# Revit family: Lighting-ArredoUrbano-GEWISS-EXTRO-BASE_COLONNA
name_source: partatom
category: Apparecchi per illuminazione
units: mm (PartAtom-declared; Revit-internal decimal feet)

## family parameters
Basato su piano di lavoro = Sì
Condiviso = No
Numero OmniClass = 23.80.00.00
Punto di calcolo locali = Sì
Quota connettore circolare = Usa diametro
Sempre verticale = Sì
Sorgente d'illuminazione = No
Taglio con vuoti quando caricato = No
Tipo di parte = Normale
Titolo OmniClass = Electric Power and Lighting

## types (1)
- GW82297 - BASE RETTANGOLARE COLONNA EXTRO G.GRAF.
    Altezza piede = 358 mm  [stored 1.17454 ft]
    Basamento = <Per categoria>
    Catalogo = LIGHTING
    Catalogo Serie = EXTRO
    Codice EAN = 8011564210431
    Codice Electrocod = 240
    Colore = Grigio grafite
    Descrizione = BASE RETTANGOLARE COLONNA EXTRO GRIGIO
    Dim. esterne BxHxP (mm) = 300x202x315
    Dimensioni AxBxC (mm) = 300x202x315
    IDF = f907310b-761a-454e-8ab0-a7a655ef85ca
    IDT = 1fff9009-d007-4e18-9cb8-e6882bacfd6c
    Immagine tipo = GW82297.jpg
    Larghezza_basamento = 202 mm  [stored 0.66273 ft]
    Lunghezza_Basamento = 300 mm  [stored 0.984252 ft]
    Lunghezza_piede = 140 mm  [stored 0.459318 ft]
    Materiale = Alluminio estruso
    Modello = GW82297
    Piede = <Per categoria>
    Produttore = GEWISS S.p.A.
    Prospetto di default = 1219 mm
    SEO = Base colonna
    Scheda Tecnica = https://www.gewiss.com
    URL = https://www.gewiss.com
    Versione file RFA = 20.11

note: [stored X ft] marks values corroborated as IEEE doubles in the binary element streams (Revit-internal decimal feet)

## geometry (parser evidence)
native form markers: Blend x2
no freeform markers — native parametric forms only
